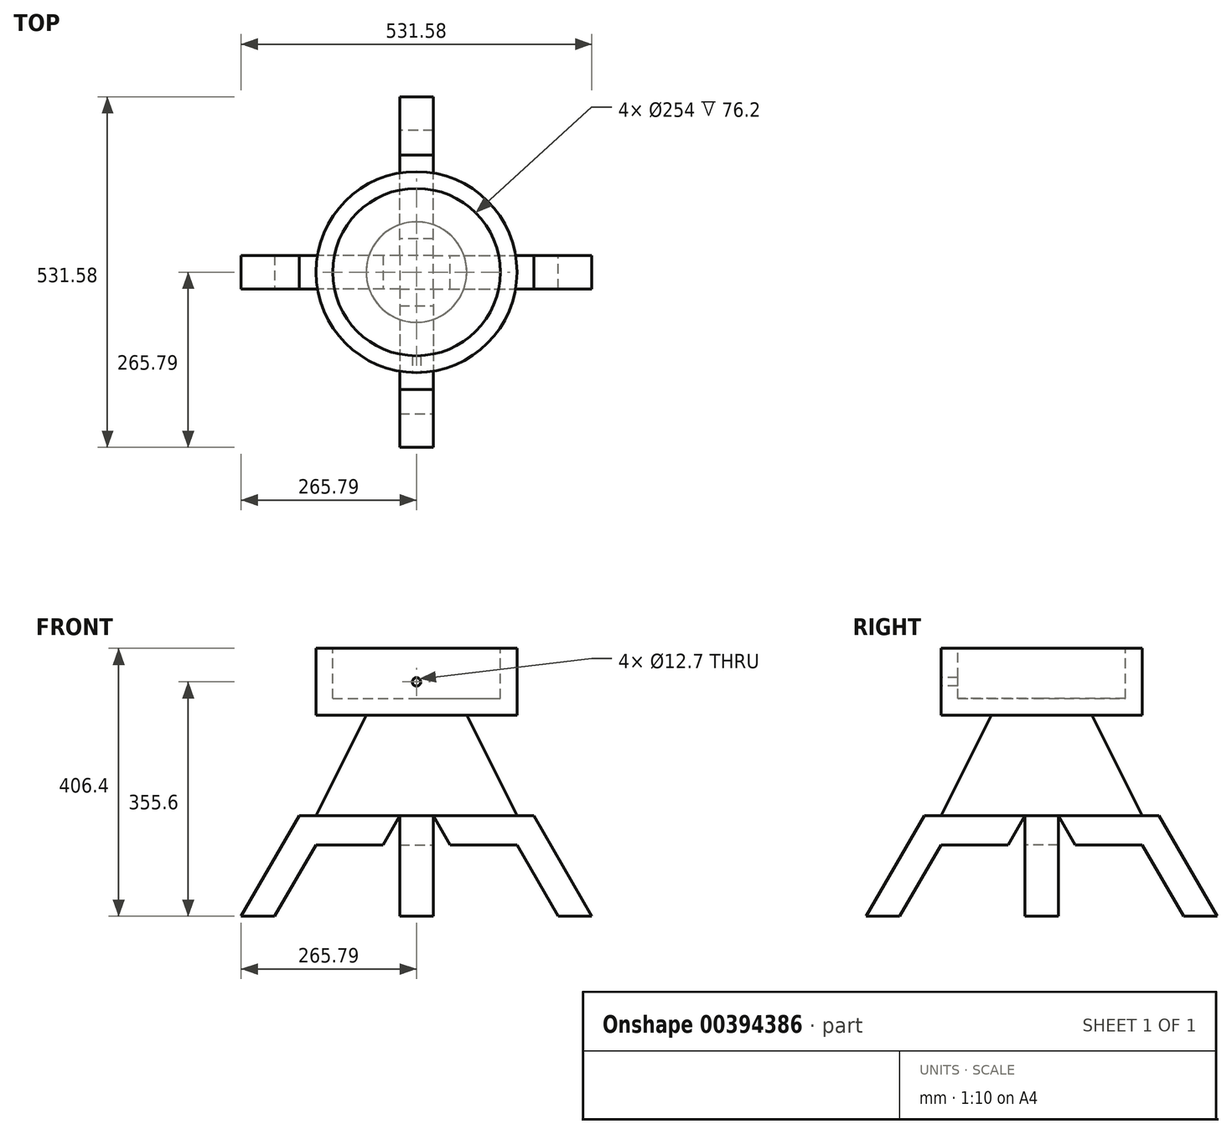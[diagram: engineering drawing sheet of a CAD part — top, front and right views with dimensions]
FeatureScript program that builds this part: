
annotation { "Feature Type Name" : "Feature", "Feature Type Description" : "" }
export const myFeature = defineFeature(function(context is Context, id is Id, definition is map)
    precondition{}
    {
        {
            var Q0;
            Q0=qCreatedBy(makeId("Top.planeOp"),FACE);
            var sketch = newSketch(context, id + "F0", { "sketchPlane" : qUnion([Q0])});
            skCircle(sketch, "E0", {"center": v(0, 0) * mm, "radius": 152.4 * mm});
            skSolve(sketch);
        }
        {
            var Q0;
            Q0=makeQuery(id+"F0.imprint","IMPRINT",FACE,{"disambiguationData":[TD([[makeQuery(id+"F0.imprint","IMPRINT",EDGE,{"derivedFrom":sQuery(id+"F0.wireOp",EDGE,"E0")}),1.0]])]});
            cPlane(context, id + "F1", {"entities" : qUnion([Q0]), "cplaneType" : CPlaneType.OFFSET, "offset" : 152.4 * mm, "width" : 152.4 * mm, "height" : 152.4 * mm});
        }
        {
            var Q0;
            Q0=qCreatedBy(id+"F1.planeOp",FACE);
            var sketch = newSketch(context, id + "F2", { "sketchPlane" : qUnion([Q0])});
            skCircle(sketch, "E1", {"center": v(0, 0) * mm, "radius": 76.2 * mm});
            skSolve(sketch);
        }
        {
            var Q0;
            Q0=makeQuery(id+"F0.imprint","IMPRINT",FACE,{"disambiguationData":[TD([[makeQuery(id+"F0.imprint","IMPRINT",EDGE,{"derivedFrom":sQuery(id+"F0.wireOp",EDGE,"E0")}),1.0]])]});
            var Q1;
            Q1=makeQuery(id+"F2.imprint","IMPRINT",FACE,{"disambiguationData":[TD([[makeQuery(id+"F2.imprint","IMPRINT",EDGE,{"derivedFrom":sQuery(id+"F2.wireOp",EDGE,"E1")}),1.0]])]});
            loft(context, id + "F3", {"sheetProfilesArray" : [{ "sheetProfileEntities" : qUnion([Q0]) }, { "sheetProfileEntities" : qUnion([Q1]) }]});
        }
        {
            var Q0;
            Q0=qCreatedBy(id+"F1.planeOp",FACE);
            var sketch = newSketch(context, id + "F4", { "sketchPlane" : qUnion([Q0])});
            skCircle(sketch, "E2", {"center": v(0, 0) * mm, "radius": 152.4 * mm});
            skSolve(sketch);
        }
        {
            var Q0;
            Q0=qCreatedBy(makeId("Right.planeOp"),FACE);
            var sketch = newSketch(context, id + "F5", { "sketchPlane" : qUnion([Q0])});
            skLineSegment(sketch, "E3", {"start": v(0, 152.4) * mm, "end": v(0, 254) * mm});
            skLineSegment(sketch, "E4", {"start": v(0, 152.4) * mm, "end": v(-152.4, 152.4) * mm});
            skLineSegment(sketch, "E5", {"start": v(0, 254) * mm, "end": v(-152.4, 254) * mm});
            skLineSegment(sketch, "E6", {"start": v(-152.4, 254) * mm, "end": v(-152.4, 152.4) * mm});
            skSolve(sketch);
        }
        {
            var Q0;
            Q0=makeQuery(id+"F5.imprint","IMPRINT",FACE,{"disambiguationData":[TD([[makeQuery(id+"F5.imprint","IMPRINT",EDGE,{"derivedFrom":sQuery(id+"F5.wireOp",EDGE,"E3")}),1.0]])]});
            var Q1;
            Q1=sQuery(id+"F5.wireOp",EDGE,"E3");
            revolve(context, id + "F6", {"operationType" : NewBodyOperationType.ADD, "entities" : qUnion([Q0]), "axis" : qUnion([Q1]), "revolveType" : RevolveType.FULL});
        }
        {
            var Q0;
            Q0=makeQuery(id+"F6.opRevolve","SWEPT_FACE",FACE,{"disambiguationData":[OSD([sQuery(id+"F5.wireOp",EDGE,"E5")])]});
            var sketch = newSketch(context, id + "F7", { "sketchPlane" : qUnion([Q0])});
            skCircle(sketch, "E7", {"center": v(0, 0) * mm, "radius": 127 * mm});
            skSolve(sketch);
        }
        {
            var Q0;
            Q0=makeQuery(id+"F7.imprint","IMPRINT",FACE,{"disambiguationData":[TD([[makeQuery(id+"F7.imprint","IMPRINT",EDGE,{"derivedFrom":sQuery(id+"F7.wireOp",EDGE,"E7")}),1.0]])]});
            extrude(context, id + "F8", {"entities" : qUnion([Q0]), "operationType" : NewBodyOperationType.REMOVE, "oppositeDirection" : true, "depth" : 76.2 * mm});
        }
        {
            var Q0;
            Q0=qCreatedBy(makeId("Front.planeOp"),FACE);
            var sketch = newSketch(context, id + "F9", { "sketchPlane" : qUnion([Q0])});
            skLineSegment(sketch, "E8", {"start": v(25.4, 0) * mm, "end": v(177.8, 0) * mm});
            skLineSegment(sketch, "E9", {"start": v(25.4, 0) * mm, "end": v(50.8, -44) * mm});
            skLineSegment(sketch, "E10", {"start": v(177.8, 0) * mm, "end": v(265.79, -152.4) * mm});
            skLineSegment(sketch, "E11", {"start": v(265.79, -152.4) * mm, "end": v(214.99, -152.4) * mm});
            skLineSegment(sketch, "E12", {"start": v(50.8, -44) * mm, "end": v(152.4, -44) * mm});
            skLineSegment(sketch, "E13", {"start": v(152.4, -44) * mm, "end": v(214.99, -152.4) * mm});
            skSolve(sketch);
        }
        {
            var Q0;
            Q0=makeQuery(id+"F9.imprint","IMPRINT",FACE,{"disambiguationData":[TD([[makeQuery(id+"F9.imprint","IMPRINT",EDGE,{"derivedFrom":sQuery(id+"F9.wireOp",EDGE,"E8")}),-1.0]])]});
            extrude(context, id + "F10", {"entities" : qUnion([Q0]), "operationType" : NewBodyOperationType.ADD, "endBound" : BoundingType.SYMMETRIC, "depth" : 50.8 * mm});
        }
        {
            var Q0;
            Q0=makeQuery(id+"F3.opLoft","SWEPT_BODY",BODY,{"disambiguationData":[OSD([makeQuery(id+"F0.imprint","IMPRINT",FACE,{"disambiguationData":[TD([[makeQuery(id+"F0.imprint","IMPRINT",EDGE,{"derivedFrom":sQuery(id+"F0.wireOp",EDGE,"E0")}),1.0]])]}),makeQuery(id+"F2.imprint","IMPRINT",FACE,{"disambiguationData":[TD([[makeQuery(id+"F2.imprint","IMPRINT",EDGE,{"derivedFrom":sQuery(id+"F2.wireOp",EDGE,"E1")}),1.0]])]})])]});
            var Q1;
            Q1=makeQuery(id+"F3.opLoft","SWEPT_FACE",FACE,{"disambiguationData":[OSD([sQuery(id+"F0.wireOp",EDGE,"E0"),sQuery(id+"F2.wireOp",EDGE,"E1")])]});
            circularPattern(context, id + "F11", {"entities" : qUnion([Q0]), "axis" : qUnion([Q1]), "angle" : 360 * degree, "instanceCount" : 4, "equalSpace" : true});
        }
        {
            var Q0;
            Q0=qCreatedBy(makeId("Front.planeOp"),FACE);
            cPlane(context, id + "F12", {"entities" : qUnion([Q0]), "cplaneType" : CPlaneType.OFFSET, "offset" : 152.4 * mm, "width" : 152.4 * mm, "height" : 152.4 * mm});
        }
        {
            var Q0;
            Q0=qCreatedBy(id+"F12.planeOp",FACE);
            var sketch = newSketch(context, id + "F13", { "sketchPlane" : qUnion([Q0])});
            skCircle(sketch, "E14", {"center": v(0, 203.2) * mm, "radius": 6.35 * mm});
            skLineSegment(sketch, "E15", {"start": v(0, 203.2) * mm, "end": v(0, 0) * mm});
            skSolve(sketch);
        }
        {
            var Q0;
            Q0=makeQuery(id+"F13.imprint","IMPRINT",FACE,{"disambiguationData":[TD([[makeQuery(id+"F13.imprint","IMPRINT",EDGE,{"derivedFrom":sQuery(id+"F13.wireOp",EDGE,"E14")}),1.0]])]});
            extrude(context, id + "F14", {"entities" : qUnion([Q0]), "operationType" : NewBodyOperationType.REMOVE, "oppositeDirection" : true, "depth" : 50.8 * mm});
        }
    });
